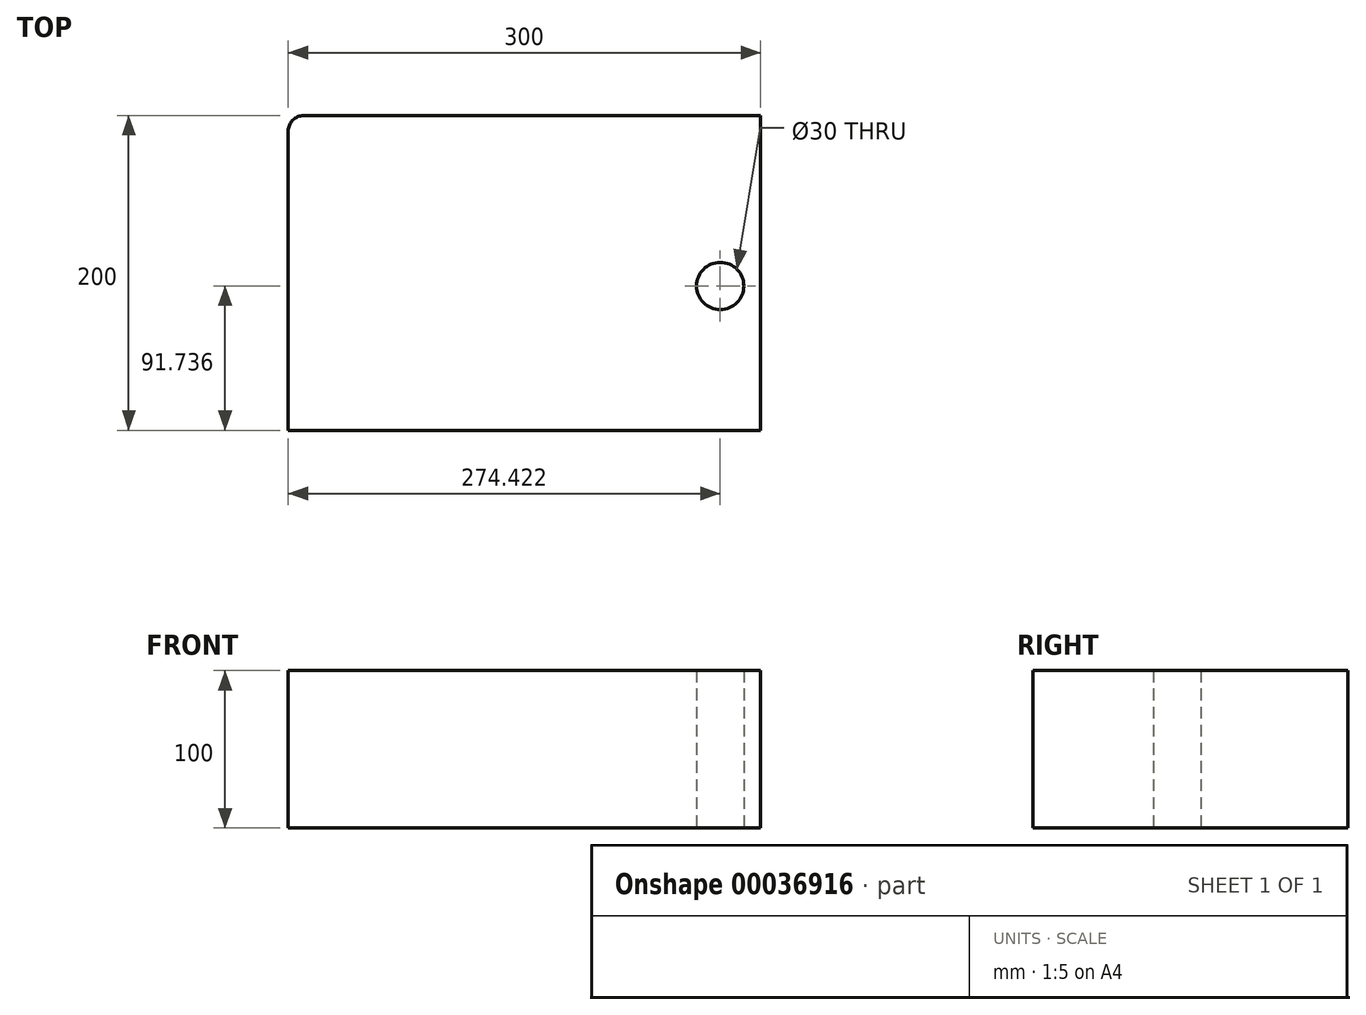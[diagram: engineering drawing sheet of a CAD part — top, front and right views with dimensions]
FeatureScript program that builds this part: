
annotation { "Feature Type Name" : "Feature", "Feature Type Description" : "" }
export const myFeature = defineFeature(function(context is Context, id is Id, definition is map)
    precondition{}
    {
        {
            var Q0;
            Q0=qCreatedBy(makeId("Top.planeOp"),FACE);
            var sketch = newSketch(context, id + "F0", { "sketchPlane" : qUnion([Q0])});
            skLineSegment(sketch, "E0.bottom", {"start": v(-140.47, 121.33) * mm, "end": v(159.53, 121.33) * mm});
            skLineSegment(sketch, "E0.top", {"start": v(-140.47, -78.67) * mm, "end": v(159.53, -78.67) * mm});
            skLineSegment(sketch, "E0.left", {"start": v(-140.47, 121.33) * mm, "end": v(-140.47, -78.67) * mm});
            skLineSegment(sketch, "E0.right", {"start": v(159.53, 121.33) * mm, "end": v(159.53, -78.67) * mm});
            skCircle(sketch, "E1", {"center": v(133.95, 13.07) * mm, "radius": 15 * mm});
            skSolve(sketch);
        }
        {
            var Q0;
            Q0=makeQuery(id+"F0.imprint","IMPRINT",FACE,{"disambiguationData":[TD([[makeQuery(id+"F0.imprint","IMPRINT",EDGE,{"derivedFrom":sQuery(id+"F0.wireOp",EDGE,"E0.bottom")}),-1.0]])]});
            extrude(context, id + "F1", {"entities" : qUnion([Q0]), "depth" : 100 * mm});
        }
        {
            var Q0;
            Q0=makeQuery(id+"F1.opExtrude","SWEPT_EDGE",EDGE,{"disambiguationData":[OSD([sQuery(id+"F0.wireOp",EDGE,"E0.bottom"),sQuery(id+"F0.wireOp",EDGE,"E0.left")])]});
            fillet(context, id + "F2", {"entities" : qUnion([Q0]), "radius" : 10 * mm, "tangentPropagation" : true, "allowEdgeOverflow" : false});
        }
    });
